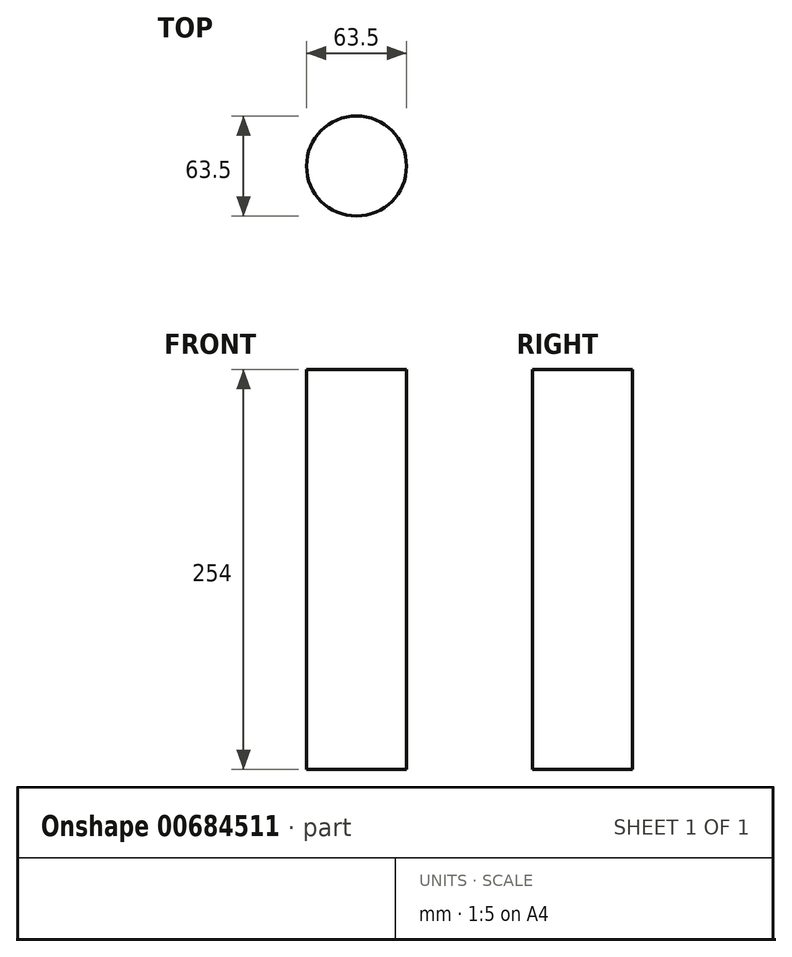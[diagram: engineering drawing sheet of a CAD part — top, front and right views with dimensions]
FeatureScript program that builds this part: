
annotation { "Feature Type Name" : "Feature", "Feature Type Description" : "" }
export const myFeature = defineFeature(function(context is Context, id is Id, definition is map)
    precondition{}
    {
        {
            var Q0;
            Q0=qCreatedBy(makeId("Top.planeOp"),FACE);
            var sketch = newSketch(context, id + "F0", { "sketchPlane" : qUnion([Q0])});
            skCircle(sketch, "E0", {"center": v(0, 0) * mm, "radius": 31.75 * mm});
            skSolve(sketch);
        }
        {
            var Q0;
            Q0=makeQuery(id+"F0.imprint","IMPRINT",FACE,{"disambiguationData":[TD([[makeQuery(id+"F0.imprint","IMPRINT",EDGE,{"derivedFrom":sQuery(id+"F0.wireOp",EDGE,"E0")}),1.0]])]});
            extrude(context, id + "F1", {"entities" : qUnion([Q0]), "depth" : 254 * mm, "offsetDistance" : 25.4 * mm});
        }
    });
